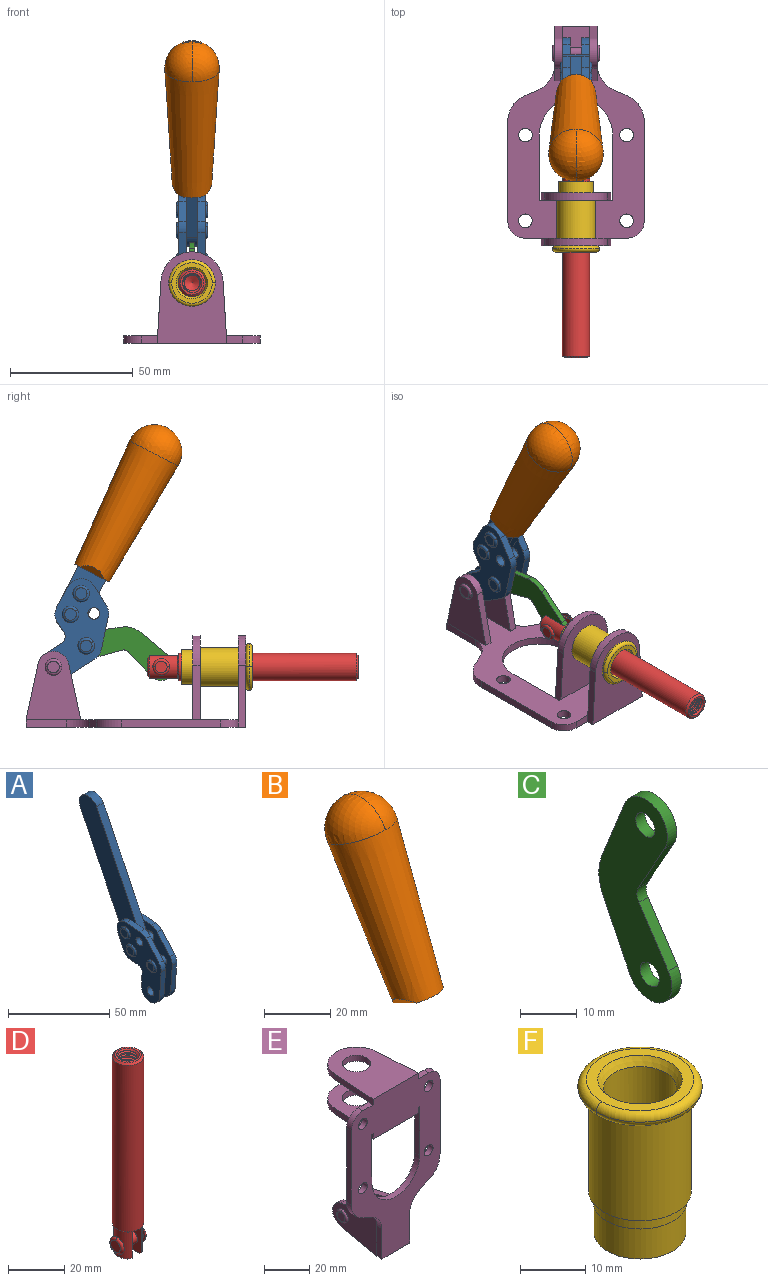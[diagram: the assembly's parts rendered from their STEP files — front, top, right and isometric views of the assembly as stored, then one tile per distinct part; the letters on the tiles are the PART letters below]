
ASSEMBLY  parts=6 mates=6
PART A: 59 faces, bbox 12.9x60.2x99.6 mm
  f0: torus R=2.39mm, axis (-1,0,0), area 14.9mm2, adj f20,f43,f51
  f1: torus R=2.39mm, axis (-1,0,0), area 14.9mm2, adj f19,f42,f51
  f2: torus R=2.39mm, axis (-1,0,0), area 14.9mm2, adj f18,f35,f51
  f3: torus R=2.39mm, axis (-1,0,0), area 14.9mm2, adj f14,f17,f23
  f4: torus R=2.39mm, axis (-1,0,0), area 14.9mm2, adj f13,f16,f23
  f5: torus R=2.39mm, axis (-1,0,0), area 14.9mm2, adj f12,f15,f23
  f6: cylinder r=2.39mm len=4.78mm, axis (1,0,0), area 46.5mm2, adj f48,f50,f51
  f7: cylinder r=2.39mm len=4.78mm, axis (1,0,0), area 46.5mm2, adj f50,f51
  f8: cylinder r=6.35mm len=12.68mm, axis (1,0,0), area 61.8mm2, adj f38,f39,f50,f51
  f9: cylinder r=2.39mm len=4.78mm, axis (-1,0,0), area 70.5mm2, adj f46,f50
  f10: cylinder r=2.39mm len=4.78mm, axis (-1,0,0), area 46.5mm2, adj f23,f45,f46
  f11: cylinder r=2.39mm len=4.78mm, axis (-1,0,0), area 46.5mm2, adj f23,f46
  f12: plane 4.78x4.78mm, normal (1,0,0), area 17.9mm2, adj f5,f15
  f13: plane 4.78x4.78mm, normal (1,0,0), area 17.9mm2, adj f4,f16
  f14: plane 4.78x4.78mm, normal (1,0,0), area 17.9mm2, adj f3,f17
  f15: torus R=2.39mm, axis (-1,0,0), area 14.9mm2, adj f5,f12,f23
  f16: torus R=2.39mm, axis (-1,0,0), area 14.9mm2, adj f4,f13,f23
  f17: torus R=2.39mm, axis (-1,0,0), area 14.9mm2, adj f3,f14,f23
  f18: plane 4.78x4.78mm, normal (-1,0,0), area 17.9mm2, adj f2,f35
  f19: plane 4.78x4.78mm, normal (-1,0,0), area 17.9mm2, adj f1,f42
  f20: plane 4.78x4.78mm, normal (-1,0,0), area 17.9mm2, adj f0,f43
  f21: plane 2.26x0.2mm, normal (1,0,0), area 0.2mm2, adj f31,f44
  f22: plane 2.26x0.2mm, normal (-1,0,0), area 0.2mm2, adj f41,f44
  f23: plane 39.37x30.77mm, normal (1,0,0), area 565.5mm2, adj f3,f4,f5,f10,f11,f15,f16,f17
  f24: cylinder r=6.1mm len=4.15mm, axis (-1,0,0), area 14.7mm2, adj f23,f25,f32,f46
  f25: plane 10.25x9.01mm, normal (0,-0.75,0.66), area 42.3mm2, adj f23,f24,f26,f46
  f26: cylinder r=6.35mm len=4.64mm, axis (-1,0,0), area 15.6mm2, adj f23,f25,f27,f46
  f27: plane 15.84x3.1mm, normal (0,-1,-0.07), area 49.2mm2, adj f23,f26,f28,f46
  f28: cylinder r=6.35mm len=12.68mm, axis (-1,0,0), area 61.8mm2, adj f23,f27,f29,f46
  f29: plane 8.11x3.1mm, normal (0,1,0.07), area 25.2mm2, adj f23,f28,f30,f46
  f30: cylinder r=3.05mm len=3.25mm, axis (-1,0,0), area 14.8mm2, adj f23,f29,f31,f46
  f31: plane 5.99x3.1mm, normal (0,0.07,-1), area 18.6mm2, adj f21,f23,f30,f44,f46
  f32: plane 9.5x3.1mm, normal (0,-0.07,1), area 29.5mm2, adj f23,f24,f33,f46,f47
  f33: cylinder r=6.1mm len=8.63mm, axis (-1,0,0), area 39.1mm2, adj f23,f32,f34,f47
  f34: plane 8.65x3.96mm, normal (0,0.91,-0.42), area 29.5mm2, adj f23,f33,f44,f47
  f35: torus R=2.39mm, axis (-1,0,0), area 14.9mm2, adj f2,f18,f51
  f36: plane 10.25x9.01mm, normal (0,-0.75,0.66), area 42.3mm2, adj f37,f49,f50,f51
  f37: cylinder r=6.35mm len=4.64mm, axis (1,0,0), area 15.6mm2, adj f36,f38,f50,f51
  f38: plane 15.84x3.1mm, normal (0,-1,-0.07), area 49.2mm2, adj f8,f37,f50,f51
  f39: plane 8.11x3.1mm, normal (0,1,0.07), area 25.2mm2, adj f8,f40,f50,f51
  f40: cylinder r=3.05mm len=3.25mm, axis (1,0,0), area 14.8mm2, adj f39,f41,f50,f51
  f41: plane 5.99x3.1mm, normal (0,0.07,-1), area 18.6mm2, adj f22,f40,f44,f50,f51
  f42: torus R=2.39mm, axis (-1,0,0), area 14.9mm2, adj f1,f19,f51
  f43: torus R=2.39mm, axis (-1,0,0), area 14.9mm2, adj f0,f20,f51
  f44: cylinder r=6.35mm len=12.12mm, axis (-1,0,0), area 128.9mm2, adj f21,f22,f23,f31,f34,f41,f46,f47
  f45: plane 2.65x1.35mm, normal (1,0,0), area 1mm2, adj f10,f55
  f46: plane 39.08x20.42mm, normal (-1,0,0), area 412.5mm2, adj f9,f10,f11,f24,f25,f26,f27,f28
  f47: plane 77.62x39.82mm, normal (1,0,0), area 850mm2, adj f32,f33,f34,f44,f53,f54,f55
  f48: plane 2.65x1.35mm, normal (-1,0,0), area 1mm2, adj f6,f55
  f49: cylinder r=6.1mm len=4.15mm, axis (1,0,0), area 14.7mm2, adj f36,f50,f51,f56
  f50: plane 39.08x20.42mm, normal (1,0,0), area 412.5mm2, adj f6,f7,f8,f9,f36,f37,f38,f39
  f51: plane 39.37x30.77mm, normal (-1,0,0), area 565.5mm2, adj f0,f1,f2,f6,f7,f8,f35,f36
  f52: plane 8.65x3.96mm, normal (0,0.91,-0.42), area 29.5mm2, adj f44,f51,f57,f58
  f53: plane 68.49x33.4mm, normal (0,0.9,-0.44), area 358.1mm2, adj f44,f47,f54,f58
  f54: cylinder r=6.35mm len=12.06mm, axis (1,0,0), area 93.7mm2, adj f47,f53,f55,f58
  f55: plane 68.49x33.4mm, normal (0,-0.9,0.44), area 358.1mm2, adj f44,f45,f46,f47,f48,f50,f54,f58
  f56: plane 9.5x3.1mm, normal (0,-0.07,1), area 29.5mm2, adj f49,f50,f51,f57,f58
  f57: cylinder r=6.1mm len=8.63mm, axis (1,0,0), area 39.1mm2, adj f51,f52,f56,f58
  f58: plane 77.62x39.82mm, normal (-1,0,0), area 850mm2, adj f44,f52,f53,f54,f55,f56,f57
PART B: 11 faces, bbox 22.3x42.6x64.5 mm
  f0: sphere r=11.13mm, area 411.4mm2, adj f1,f8
  f1: cone r=11.11mm half-angle=3.3deg, axis (0,0.44,0.9), area 3251.8mm2, adj f0,f7,f8,f9,f10
  f2: cylinder r=6.16mm len=11.7mm, axis (1,0,0), area 89.5mm2, adj f3,f4,f5,f6
  f3: plane 60.23x36.75mm, normal (-1,0,0), area 763.6mm2, adj f2,f4,f6,f10
  f4: plane 51.37x25.05mm, normal (0,0.9,-0.44), area 264.2mm2, adj f2,f3,f5,f10
  f5: plane 60.23x36.75mm, normal (1,0,0), area 763.6mm2, adj f2,f4,f6,f10
  f6: plane 51.37x25.05mm, normal (0,-0.9,0.44), area 264.2mm2, adj f2,f3,f5,f10
  f7: plane 9.95x5.95mm, normal (0.71,-0.31,-0.64), area 25.8mm2, adj f1,f10
  f8: sphere r=11.13mm, area 411.4mm2, adj f0,f1
  f9: plane 9.95x5.95mm, normal (-0.71,-0.31,-0.64), area 25.8mm2, adj f1,f10
  f10: plane 14.27x11.38mm, normal (0,-0.44,-0.9), area 106.7mm2, adj f1,f3,f4,f5,f6,f7,f9
PART C: 12 faces, bbox 2.3x18.2x42.8 mm
  f0: cylinder r=2.4mm len=4.8mm, axis (1,0,0), area 34.9mm2, adj f4,f11
  f1: cylinder r=10.41mm len=8.47mm, axis (1,0,0), area 20.2mm2, adj f4,f9,f10,f11
  f2: cylinder r=3.05mm len=3.16mm, axis (1,0,0), area 7.7mm2, adj f4,f6,f7,f11
  f3: cylinder r=2.4mm len=4.8mm, axis (1,0,0), area 34.9mm2, adj f4,f11
  f4: plane 42.81x18.23mm, normal (-1,0,0), area 414.1mm2, adj f0,f1,f2,f3,f5,f6,f7,f8
  f5: cylinder r=5.54mm len=10.67mm, axis (1,0,0), area 41.8mm2, adj f4,f6,f10,f11
  f6: plane 11.66x6.53mm, normal (0,-0.87,-0.49), area 30.9mm2, adj f2,f4,f5,f11
  f7: plane 11.17x7.33mm, normal (0,-0.84,0.55), area 30.9mm2, adj f2,f4,f8,f11
  f8: cylinder r=5.54mm len=10.51mm, axis (1,0,0), area 41.8mm2, adj f4,f7,f9,f11
  f9: plane 13.67x6.67mm, normal (0,0.9,-0.44), area 35.1mm2, adj f1,f4,f8,f11
  f10: plane 14.1x5.7mm, normal (0,0.93,0.37), area 35.1mm2, adj f1,f4,f5,f11
  f11: plane 42.81x18.23mm, normal (1,0,0), area 414.1mm2, adj f0,f1,f2,f3,f5,f6,f7,f8
PART D: 48 faces, bbox 12.6x11.1x86.1 mm
  f0: torus R=2.41mm, axis (-1,0,0), area 15mm2, adj f30,f32,f34
  f1: torus R=2.41mm, axis (-1,0,0), area 15mm2, adj f29,f31,f33
  f2: cylinder r=5.54mm len=72.39mm, axis (0,0,1), area 2518.5mm2, adj f3,f4,f42,f43
  f3: cone r=5.54mm half-angle=45deg, axis (0,0,1), area 7.6mm2, adj f2,f5,f41
  f4: cone r=5.54mm half-angle=45deg, axis (0,0,-1), area 34.9mm2, adj f2,f39
  f5: cylinder r=5.08mm len=11.48mm, axis (0,0,1), area 108.3mm2, adj f3,f7,f8,f41
  f6: cylinder r=2.41mm len=4.83mm, axis (-1,0,0), area 71.2mm2, adj f40,f41
  f7: cylinder r=2.41mm len=4.83mm, axis (-1,0,0), area 7.6mm2, adj f5,f34
  f8: cone r=5.08mm half-angle=45deg, axis (0,0,1), area 10.6mm2, adj f5,f37,f41
  f9: cone r=3.98mm half-angle=45deg, axis (0,0,1), area 17.6mm2, adj f27,f39,f45,f46,f47
  f10: cylinder r=2.41mm len=4.83mm, axis (-1,0,0), area 7.6mm2, adj f33,f38
  f11: cylinder r=3.2mm len=6.4mm, axis (0,0,1), area 78.4mm2, adj f12,f28,f44,f45,f47
  f12: cylinder r=3.2mm len=6.4mm, axis (0,0,1), area 10.5mm2, adj f11,f13,f45,f47
  f13: cylinder r=3.2mm len=6.4mm, axis (0,0,1), area 10.5mm2, adj f12,f14,f45,f47
  f14: cylinder r=3.2mm len=6.4mm, axis (0,0,1), area 10.5mm2, adj f13,f15,f45,f47
  f15: cylinder r=3.2mm len=6.4mm, axis (0,0,1), area 10.5mm2, adj f14,f16,f45,f47
  f16: cylinder r=3.2mm len=6.4mm, axis (0,0,1), area 10.5mm2, adj f15,f17,f45,f47
  f17: cylinder r=3.2mm len=6.4mm, axis (0,0,1), area 10.5mm2, adj f16,f18,f45,f47
  f18: cylinder r=3.2mm len=6.4mm, axis (0,0,1), area 10.5mm2, adj f17,f19,f45,f47
  f19: cylinder r=3.2mm len=6.4mm, axis (0,0,1), area 10.5mm2, adj f18,f20,f45,f47
  f20: cylinder r=3.2mm len=6.4mm, axis (0,0,1), area 10.5mm2, adj f19,f21,f45,f47
  f21: cylinder r=3.2mm len=6.4mm, axis (0,0,1), area 10.5mm2, adj f20,f22,f45,f47
  f22: cylinder r=3.2mm len=6.4mm, axis (0,0,1), area 10.5mm2, adj f21,f23,f45,f47
  f23: cylinder r=3.2mm len=6.4mm, axis (0,0,1), area 10.5mm2, adj f22,f24,f45,f47
  f24: cylinder r=3.2mm len=6.4mm, axis (0,0,1), area 10.5mm2, adj f23,f25,f45,f47
  f25: cylinder r=3.2mm len=6.4mm, axis (0,0,1), area 10.5mm2, adj f24,f26,f45,f47
  f26: cylinder r=3.2mm len=6.4mm, axis (0,0,1), area 10.5mm2, adj f25,f27,f45,f47
  f27: cylinder r=3.2mm len=6.4mm, axis (0,0,1), area 7.4mm2, adj f9,f26,f45,f47
  f28: cone r=3.2mm half-angle=60deg, axis (0,0,1), area 37.2mm2, adj f11
  f29: plane 4.83x4.83mm, normal (-1,0,0), area 18.3mm2, adj f1,f31
  f30: plane 4.83x4.83mm, normal (1,0,0), area 18.3mm2, adj f0,f32
  f31: torus R=2.41mm, axis (-1,0,0), area 15mm2, adj f1,f29,f33
  f32: torus R=2.41mm, axis (-1,0,0), area 15mm2, adj f0,f30,f34
  f33: plane 6.83x6.83mm, normal (1,0,0), area 18.3mm2, adj f1,f10,f31
  f34: plane 6.83x6.83mm, normal (-1,0,0), area 18.3mm2, adj f0,f7,f32
  f35: cone r=5.08mm half-angle=45deg, axis (0,0,1), area 10.6mm2, adj f36,f38,f40
  f36: plane 7.25x1.97mm, normal (0,0,-1), area 10mm2, adj f35,f40
  f37: plane 7.25x1.97mm, normal (0,0,-1), area 10mm2, adj f8,f41
  f38: cylinder r=5.08mm len=11.48mm, axis (0,0,1), area 108.3mm2, adj f10,f35,f40,f42
  f39: plane 9.55x9.55mm, normal (0,0,1), area 22mm2, adj f4,f9
  f40: plane 12.76x10.09mm, normal (1,0,0), area 95.7mm2, adj f6,f35,f36,f38,f42,f43
  f41: plane 12.76x10.09mm, normal (-1,0,0), area 95.7mm2, adj f3,f5,f6,f8,f37,f43
  f42: cone r=5.54mm half-angle=45deg, axis (0,0,1), area 7.6mm2, adj f2,f38,f40
  f43: plane 11.07x4.7mm, normal (0,0,-1), area 50.4mm2, adj f2,f40,f41
  f44: plane 0.89x0.62mm, normal (-1,0,0), area 0.3mm2, adj f11,f45,f46,f47
  f45: bspline ~24.8x7.63mm, area 266.6mm2, adj f9,f11,f12,f13,f14,f15,f16,f17
  f46: bspline ~24.87x7.63mm, area 73.6mm2, adj f9,f44,f45,f47
  f47: bspline ~24.98x7.63mm, area 272.5mm2, adj f9,f11,f12,f13,f14,f15,f16,f17
PART E: 55 faces, bbox 55.7x37.4x89.8 mm
  f0: torus R=2.41mm, axis (-1,0,0), area 15mm2, adj f11,f15,f25
  f1: torus R=2.41mm, axis (-1,0,0), area 15mm2, adj f10,f12,f22
  f2: cylinder r=2.78mm len=5.56mm, axis (0,-1,0), area 54.2mm2, adj f30,f54
  f3: cylinder r=14.99mm len=29.97mm, axis (0,-1,0), area 145.9mm2, adj f30,f49,f53,f54
  f4: cylinder r=2.78mm len=5.56mm, axis (0,-1,0), area 54.2mm2, adj f30,f54
  f5: cylinder r=2.78mm len=5.56mm, axis (0,-1,0), area 54.2mm2, adj f30,f54
  f6: cylinder r=2.78mm len=5.56mm, axis (0,-1,0), area 54.2mm2, adj f30,f54
  f7: cylinder r=6.35mm len=12.7mm, axis (0,0,1), area 123.6mm2, adj f27,f51
  f8: cylinder r=6.35mm len=12.7mm, axis (0,0,-1), area 124.7mm2, adj f21,f35
  f9: cylinder r=2.41mm len=11.18mm, axis (-1,0,0), area 169.4mm2, adj f16,f19
  f10: plane 4.83x4.83mm, normal (1,0,0), area 18.3mm2, adj f1,f12
  f11: plane 4.83x4.83mm, normal (-1,0,0), area 18.3mm2, adj f0,f15
  f12: torus R=2.41mm, axis (-1,0,0), area 15mm2, adj f1,f10,f22
  f13: cylinder r=6.35mm len=12.41mm, axis (1,0,0), area 53.4mm2, adj f18,f19,f22,f23
  f14: cylinder r=6.35mm len=12.41mm, axis (-1,0,0), area 53.4mm2, adj f16,f17,f24,f25
  f15: torus R=2.41mm, axis (-1,0,0), area 15mm2, adj f0,f11,f25
  f16: plane 27.86x22.35mm, normal (1,0,0), area 425.4mm2, adj f9,f14,f17,f24,f30
  f17: plane 22.86x4.97mm, normal (0,0.21,0.98), area 72.5mm2, adj f14,f16,f25,f30
  f18: plane 22.86x4.97mm, normal (0,0.21,0.98), area 72.5mm2, adj f13,f19,f22,f30
  f19: plane 27.86x22.35mm, normal (-1,0,0), area 425.4mm2, adj f9,f13,f18,f23,f30
  f20: cylinder r=12.7mm len=25.35mm, axis (0,0,-1), area 119.8mm2, adj f21,f34,f35,f36
  f21: plane 34.21x28.07mm, normal (0,0,-1), area 702.4mm2, adj f8,f20,f30,f34,f36
  f22: plane 27.96x22.45mm, normal (1,0,0), area 407.2mm2, adj f1,f12,f13,f18,f23,f30,f42,f43
  f23: plane 22.86x4.97mm, normal (0,0.21,-0.98), area 72.5mm2, adj f13,f19,f22,f44
  f24: plane 22.86x4.97mm, normal (0,0.21,-0.98), area 72.5mm2, adj f14,f16,f25,f44
  f25: plane 27.86x22.35mm, normal (-1,0,0), area 407.1mm2, adj f0,f14,f15,f17,f24,f30,f45,f46
  f26: plane 3.1x0.95mm, normal (0,0,-1), area 2.7mm2, adj f30,f49,f50,f54
  f27: plane 34.21x28.07mm, normal (0,0,1), area 702.4mm2, adj f7,f28,f30,f50,f52
  f28: cylinder r=12.7mm len=25.35mm, axis (0,0,1), area 118.8mm2, adj f27,f50,f51,f52
  f29: plane 3.1x0.95mm, normal (0,0,-1), area 2.7mm2, adj f30,f52,f53,f54
  f30: plane 86.54x55.63mm, normal (0,1,0), area 2362.9mm2, adj f2,f3,f4,f5,f6,f16,f17,f18
  f31: plane 40.56x3.1mm, normal (-1,0,0), area 125.7mm2, adj f30,f32,f48,f54
  f32: cylinder r=7.11mm len=7.11mm, axis (0,-1,0), area 34.6mm2, adj f30,f31,f33,f54
  f33: plane 6.67x3.1mm, normal (0,0,1), area 20.4mm2, adj f30,f32,f34,f54
  f34: plane 25.39x3.13mm, normal (-1,0.06,0), area 79.5mm2, adj f20,f21,f33,f35,f54
  f35: plane 37.31x28.45mm, normal (0,0,1), area 789.9mm2, adj f8,f20,f34,f36,f54
  f36: plane 25.39x3.13mm, normal (1,0.06,0), area 79.5mm2, adj f20,f21,f35,f37,f54
  f37: plane 6.67x3.1mm, normal (0,0,1), area 20.4mm2, adj f30,f36,f38,f54
  f38: cylinder r=7.11mm len=7.11mm, axis (0,-1,0), area 34.6mm2, adj f30,f37,f39,f54
  f39: plane 40.56x3.1mm, normal (1,0,0), area 125.7mm2, adj f30,f38,f40,f54
  f40: cylinder r=11.18mm len=10.16mm, axis (0,-1,0), area 39.5mm2, adj f30,f39,f41,f54
  f41: plane 6.09x3.1mm, normal (0.42,0,-0.91), area 20.8mm2, adj f30,f40,f42,f54
  f42: cylinder r=11.18mm len=9.41mm, axis (0,-1,0), area 37.2mm2, adj f22,f30,f41,f43,f54
  f43: plane 16.5x3.1mm, normal (1,0,0), area 51.1mm2, adj f22,f42,f44,f54
  f44: plane 17.37x3.1mm, normal (0,0,-1), area 53.8mm2, adj f23,f24,f30,f43,f45,f54
  f45: plane 16.5x3.1mm, normal (-1,0,0), area 51.1mm2, adj f25,f44,f46,f54
  f46: cylinder r=11.18mm len=9.41mm, axis (0,-1,0), area 37.2mm2, adj f25,f30,f45,f47,f54
  f47: plane 6.09x3.1mm, normal (-0.42,0,-0.91), area 20.8mm2, adj f30,f46,f48,f54
  f48: cylinder r=11.18mm len=10.16mm, axis (0,-1,0), area 39.5mm2, adj f30,f31,f47,f54
  f49: plane 26.54x3.1mm, normal (-1,0,0), area 82.3mm2, adj f3,f26,f30,f54
  f50: plane 25.39x3.1mm, normal (1,0.06,0), area 78.8mm2, adj f26,f27,f28,f51,f54
  f51: plane 37.31x28.45mm, normal (0,0,-1), area 789.9mm2, adj f7,f28,f50,f52,f54
  f52: plane 25.39x3.1mm, normal (-1,0.06,0), area 78.8mm2, adj f27,f28,f29,f51,f54
  f53: plane 26.54x3.1mm, normal (1,0,0), area 82.3mm2, adj f3,f29,f30,f54
  f54: plane 89.66x55.63mm, normal (0,-1,0), area 2678.5mm2, adj f2,f3,f4,f5,f6,f26,f29,f31
PART F: 15 faces, bbox 20.6x20.6x28.7 mm
  f0: torus R=8.26mm, axis (0,0,1), area 56.8mm2, adj f1,f10,f12
  f1: torus R=8.26mm, axis (0,0,1), area 56.8mm2, adj f0,f6,f13
  f2: cylinder r=5.59mm len=25.91mm, axis (0,0,1), area 909.6mm2, adj f3,f4
  f3: cone r=6.86mm half-angle=45deg, axis (0,0,-1), area 70.2mm2, adj f2,f14
  f4: cone r=6.47mm half-angle=30deg, axis (0,0,1), area 66.7mm2, adj f2,f13
  f5: cylinder r=7.04mm len=14.07mm, axis (0,0,1), area 252.6mm2, adj f11,f14
  f6: torus R=8.26mm, axis (0,0,1), area 56.8mm2, adj f1,f12,f13
  f7: cylinder r=7.16mm len=14.33mm, axis (0,0,1), area 91.5mm2, adj f9,f11
  f8: cylinder r=7.86mm len=18.42mm, axis (0,0,1), area 909.6mm2, adj f9,f10
  f9: plane 15.72x15.72mm, normal (0,0,-1), area 33mm2, adj f7,f8
  f10: plane 16.51x16.51mm, normal (0,0,-1), area 19.9mm2, adj f0,f8,f12
  f11: plane 14.33x14.33mm, normal (0,0,-1), area 5.7mm2, adj f5,f7
  f12: torus R=8.26mm, axis (0,0,1), area 56.8mm2, adj f0,f6,f10
  f13: plane 16.51x16.51mm, normal (0,0,1), area 82.7mm2, adj f1,f4,f6
  f14: plane 14.07x14.07mm, normal (0,0,-1), area 7.8mm2, adj f3,f5
PLACE A rot(axis=(1,0,0),53.3deg) t=(0,-7.12,24.03)mm
PLACE B rot(axis=(1,0,0),53.3deg) t=(0,-7.12,24.03)mm
PLACE C rot(axis=(1,0,0),107.7deg) t=(0,11.6,5.85)mm
PLACE D rot(axis=(1,0,0),90deg) t=(0,4.86,0)mm
PLACE E rot(axis=(1,0,0),90deg) t=(0,1.23,0)mm fixed
PLACE F rot(axis=(1,0,0),90deg) t=(0,1.23,0)mm
MATE fastened F.f2 <-> E.f7  axis (0,-1,0) through (0,-45.16,24.61)mm
MATE fastened A.f54 <-> B.f2  axis (1,0,0) through (0,-8.63,113.72)mm
MATE revolute C.f3 <-> A.f4  axis (1,0,0) through (0,19.96,33.18)mm
MATE revolute A.f7 <-> E.f0  axis (1,0,0) through (0,33.32,24.61)mm
MATE revolute C.f5 <-> D.f6  axis (1,0,0) through (0,-10.61,24.61)mm
MATE slider D.f2 <-> E.f7  axis (0,-1,0) through (0,-53.92,24.61)mm
